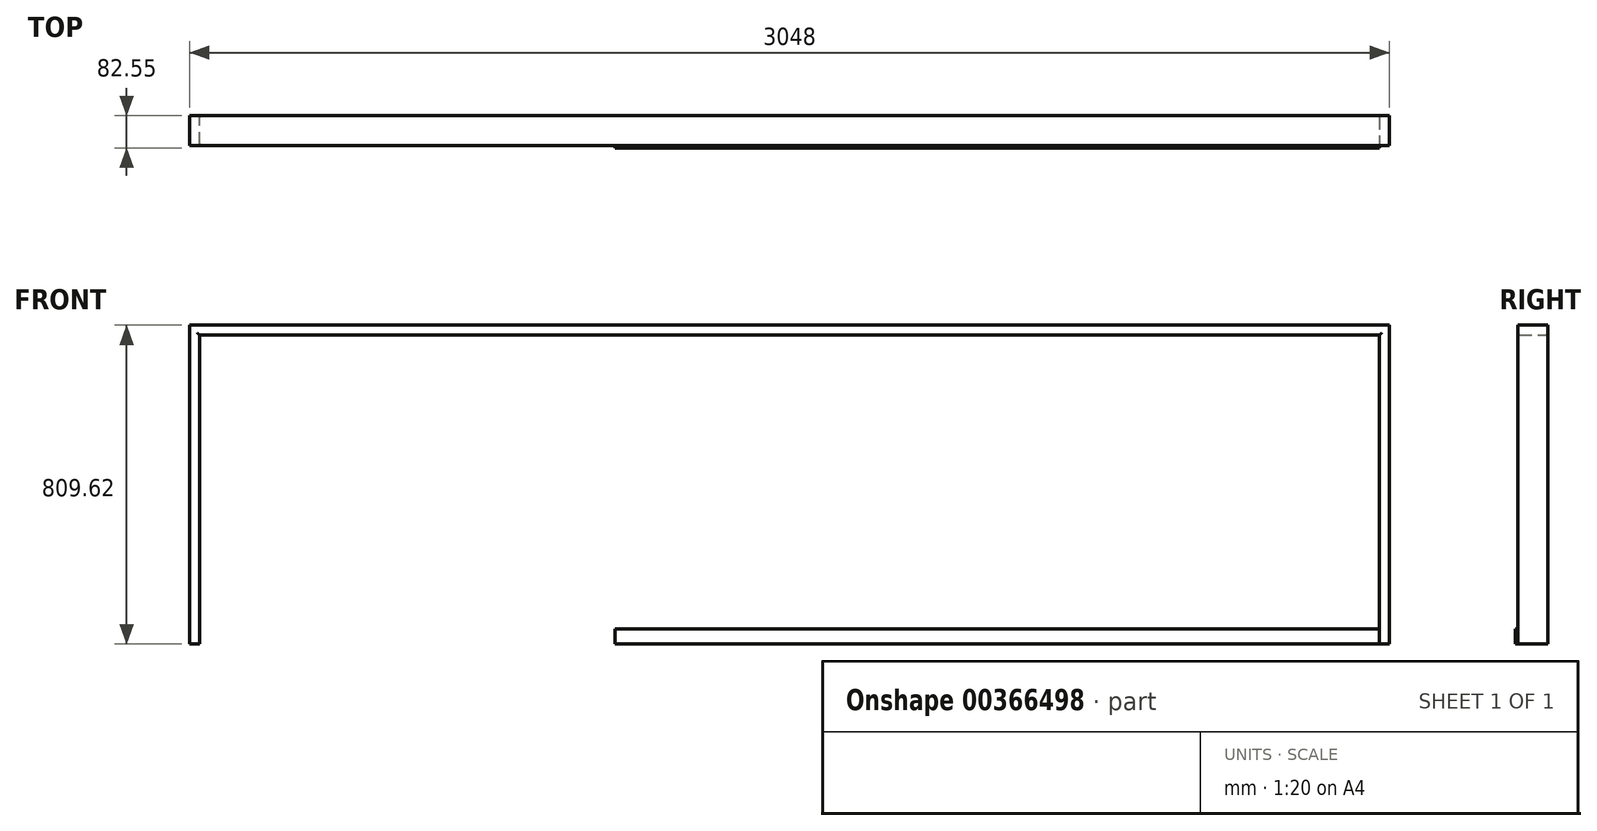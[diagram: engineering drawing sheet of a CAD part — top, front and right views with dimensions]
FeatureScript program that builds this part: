
annotation { "Feature Type Name" : "Feature", "Feature Type Description" : "" }
export const myFeature = defineFeature(function(context is Context, id is Id, definition is map)
    precondition{}
    {
        {
            var Q0;
            Q0=qCreatedBy(makeId("Front.planeOp"),FACE);
            var sketch = newSketch(context, id + "F0", { "sketchPlane" : qUnion([Q0])});
            skLineSegment(sketch, "E0", {"start": v(0, 0) * mm, "end": v(0, 809.62) * mm});
            skLineSegment(sketch, "E1", {"start": v(0, 809.62) * mm, "end": v(-3048, 809.62) * mm});
            skLineSegment(sketch, "E2", {"start": v(-3048, 809.62) * mm, "end": v(-3048, 0) * mm});
            skSolve(sketch);
        }
        {
            var Q0;
            Q0=qCreatedBy(makeId("Top.planeOp"),FACE);
            var sketch = newSketch(context, id + "F1", { "sketchPlane" : qUnion([Q0])});
            skLineSegment(sketch, "E3", {"start": v(0, 0) * mm, "end": v(-25.4, 0) * mm});
            skLineSegment(sketch, "E4", {"start": v(-25.4, 0) * mm, "end": v(-25.4, -76.2) * mm});
            skLineSegment(sketch, "E5", {"start": v(-25.4, -76.2) * mm, "end": v(0, -76.2) * mm});
            skLineSegment(sketch, "E6", {"start": v(0, -76.2) * mm, "end": v(0, 0) * mm});
            skSolve(sketch);
        }
        {
            var Q0;
            Q0=makeQuery(id+"F1.imprint","IMPRINT",FACE,{"disambiguationData":[TD([[makeQuery(id+"F1.imprint","IMPRINT",EDGE,{"derivedFrom":sQuery(id+"F1.wireOp",EDGE,"E3")}),1.0]])]});
            var Q1;
            Q1=sQuery(id+"F0.wireOp",EDGE,"E0");
            var Q2;
            Q2=sQuery(id+"F0.wireOp",EDGE,"E2");
            var Q3;
            Q3=sQuery(id+"F0.wireOp",EDGE,"E1");
            sweep(context, id + "F2", {"profiles" : qUnion([Q0]), "path" : qUnion([Q1, Q2, Q3])});
        }
        {
            var Q0;
            Q0=makeQuery(id+"F2.opSweep","SWEPT_FACE",FACE,{"disambiguationData":[OSD([sQuery(id+"F0.wireOp",EDGE,"E0"),sQuery(id+"F1.wireOp",EDGE,"E5")])]});
            var sketch = newSketch(context, id + "F3", { "sketchPlane" : qUnion([Q0])});
            skLineSegment(sketch, "E7", {"start": v(-25.4, 0) * mm, "end": v(-1966.91, 0) * mm});
            skLineSegment(sketch, "E8", {"start": v(-1966.91, 0) * mm, "end": v(-1966.91, 38.1) * mm});
            skLineSegment(sketch, "E9", {"start": v(-1966.91, 38.1) * mm, "end": v(-25.4, 38.1) * mm});
            skLineSegment(sketch, "E10", {"start": v(-25.4, 38.1) * mm, "end": v(-25.4, 0) * mm});
            skSolve(sketch);
        }
        {
            var Q0;
            Q0=makeQuery(id+"F2.opSweep","SWEPT_EDGE",EDGE,{"disambiguationData":[OSD([sQuery(id+"F0.wireOp",EDGE,"E0"),sQuery(id+"F1.wireOp",EDGE,"E3"),sQuery(id+"F1.wireOp",EDGE,"E4")])]});
            var Q1;
            Q1=makeQuery(id+"F2.opSweep","SWEPT_EDGE",EDGE,{"disambiguationData":[OSD([sQuery(id+"F0.wireOp",EDGE,"E0"),sQuery(id+"F1.wireOp",EDGE,"E4"),sQuery(id+"F1.wireOp",EDGE,"E5")])]});
            var Q2;
            Q2=makeQuery(id+"F2.opSweep","SWEPT_EDGE",EDGE,{"disambiguationData":[OSD([sQuery(id+"F0.wireOp",EDGE,"E1"),sQuery(id+"F1.wireOp",EDGE,"E3"),sQuery(id+"F1.wireOp",EDGE,"E4")])]});
            var Q3;
            Q3=makeQuery(id+"F2.opSweep","SWEPT_EDGE",EDGE,{"disambiguationData":[OSD([sQuery(id+"F0.wireOp",EDGE,"E1"),sQuery(id+"F1.wireOp",EDGE,"E4"),sQuery(id+"F1.wireOp",EDGE,"E5")])]});
            var Q4;
            Q4=makeQuery(id+"F2.opSweep","SWEPT_EDGE",EDGE,{"disambiguationData":[OSD([sQuery(id+"F0.wireOp",EDGE,"E2"),sQuery(id+"F1.wireOp",EDGE,"E3"),sQuery(id+"F1.wireOp",EDGE,"E4")])]});
            var Q5;
            Q5=makeQuery(id+"F2.opSweep","SWEPT_EDGE",EDGE,{"disambiguationData":[OSD([sQuery(id+"F0.wireOp",EDGE,"E2"),sQuery(id+"F1.wireOp",EDGE,"E4"),sQuery(id+"F1.wireOp",EDGE,"E5")])]});
            fillet(context, id + "F4", {"entities" : qUnion([Q0, Q1, Q2, Q3, Q4, Q5]), "radius" : 5.08 * mm, "tangentPropagation" : true, "allowEdgeOverflow" : false});
        }
        {
            var Q0;
            Q0=makeQuery(id+"F3.imprint","IMPRINT",FACE,{"disambiguationData":[TD([[makeQuery(id+"F3.imprint","IMPRINT",EDGE,{"derivedFrom":sQuery(id+"F3.wireOp",EDGE,"E7")}),-1.0]])]});
            extrude(context, id + "F5", {"entities" : qUnion([Q0]), "depth" : 6.35 * mm});
        }
    });
